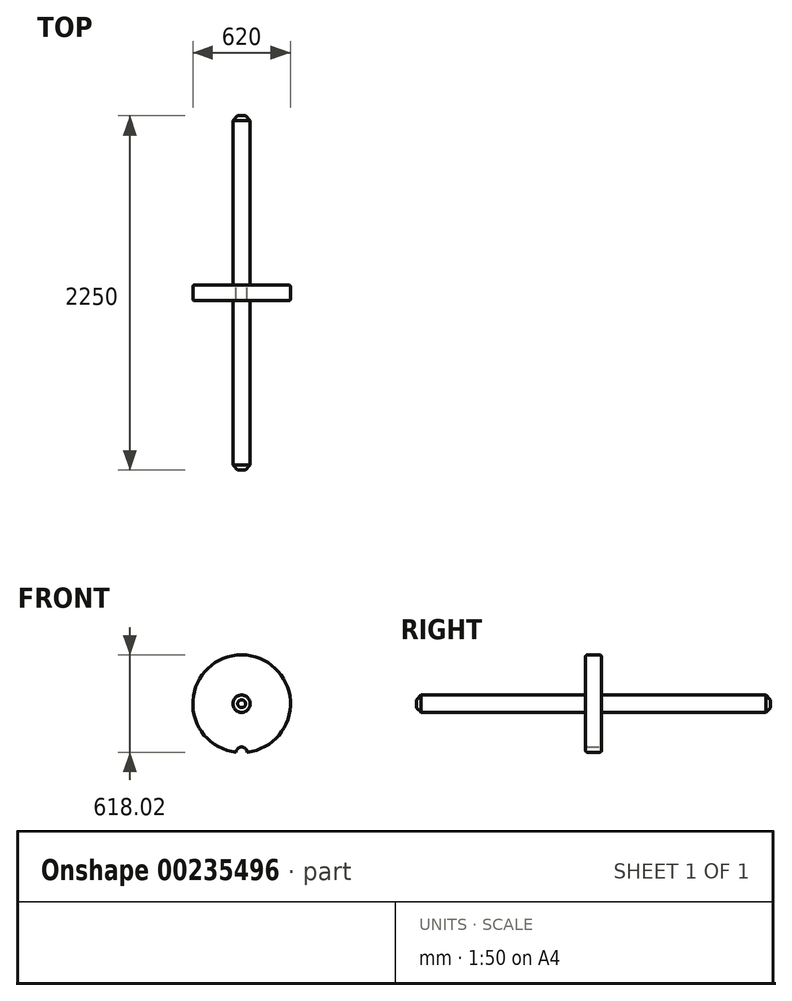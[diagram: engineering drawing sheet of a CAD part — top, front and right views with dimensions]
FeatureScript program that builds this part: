
annotation { "Feature Type Name" : "Feature", "Feature Type Description" : "" }
export const myFeature = defineFeature(function(context is Context, id is Id, definition is map)
    precondition{}
    {
        {
            var Q0;
            Q0=qCreatedBy(makeId("Front.planeOp"),FACE);
            var sketch = newSketch(context, id + "F0", { "sketchPlane" : qUnion([Q0])});
            skCircle(sketch, "E0", {"center": v(0, 0) * mm, "radius": 310 * mm});
            skCircle(sketch, "E1", {"center": v(0, 0) * mm, "radius": 55 * mm});
            skCircle(sketch, "E2", {"center": v(0, 0) * mm, "radius": 275 * mm, "construction": true});
            skSolve(sketch);
        }
        {
            var Q0;
            Q0=makeQuery(id+"F0.imprint","IMPRINT",FACE,{"disambiguationData":[TD([[makeQuery(id+"F0.imprint","IMPRINT",EDGE,{"derivedFrom":sQuery(id+"F0.wireOp",EDGE,"E0")}),1.0]])]});
            extrude(context, id + "F1", {"entities" : qUnion([Q0]), "endBound" : BoundingType.SYMMETRIC, "depth" : 100 * mm});
        }
        {
            var Q0;
            Q0=makeQuery(id+"F0.imprint","IMPRINT",FACE,{"disambiguationData":[TD([[makeQuery(id+"F0.imprint","IMPRINT",EDGE,{"derivedFrom":sQuery(id+"F0.wireOp",EDGE,"E1")}),1.0]])]});
            extrude(context, id + "F2", {"entities" : qUnion([Q0]), "operationType" : NewBodyOperationType.ADD, "endBound" : BoundingType.SYMMETRIC, "depth" : 2250 * mm});
        }
        {
            var Q0;
            Q0=makeQuery(id+"F2.opExtrude","CAP_EDGE",EDGE,{"disambiguationData":[OSD([sQuery(id+"F0.wireOp",EDGE,"E1")])],"isStart":false});
            var Q1;
            Q1=makeQuery(id+"F2.opExtrude","CAP_EDGE",EDGE,{"disambiguationData":[OSD([sQuery(id+"F0.wireOp",EDGE,"E1")])],"isStart":true});
            chamfer(context, id + "F3", {"entities" : qUnion([Q0, Q1]), "width" : 30 * mm, "tangentPropagation" : true});
        }
        {
            var Q0;
            Q0=makeQuery(id+"F1.opExtrude","CAP_FACE",FACE,{"disambiguationData":[OSD([sQuery(id+"F0.wireOp",EDGE,"E0"),sQuery(id+"F0.wireOp",EDGE,"E1")])],"isStart":true});
            var sketch = newSketch(context, id + "F4", { "sketchPlane" : qUnion([Q0])});
            skCircle(sketch, "E3", {"center": v(0, 0) * mm, "radius": 275 * mm});
            skCircle(sketch, "E4", {"center": v(0, -310) * mm, "radius": 35 * mm});
            skSolve(sketch);
        }
        {
            var Q0;
            {var subQ0=sQuery(id+"F4.wireOp",EDGE,"E4");var subQ1=makeQuery(id+"F4.imprint","INTERSECT",VERTEX,{"derivedFrom":[sQuery(id+"F4.wireOp",EDGE,"E3"),subQ0]});Q0=makeQuery(id+"F4.imprint","IMPRINT",FACE,{"disambiguationData":[TD([[makeQuery(id+"F4.imprint","IMPRINT",EDGE,{"disambiguationData":[TD([[subQ1,1.0]])],"derivedFrom":subQ0}),1.0]])]});}
            extrude(context, id + "F5", {"entities" : qUnion([Q0]), "operationType" : NewBodyOperationType.REMOVE, "oppositeDirection" : true, "depth" : 100 * mm});
        }
        {
            var Q0;
            Q0=makeQuery(id+"F1.opExtrude","CAP_FACE",FACE,{"disambiguationData":[OSD([sQuery(id+"F0.wireOp",EDGE,"E0"),sQuery(id+"F0.wireOp",EDGE,"E1")])],"isStart":true});
            fillet(context, id + "F6", {"entities" : qUnion([Q0]), "radius" : 10 * mm, "tangentPropagation" : true, "allowEdgeOverflow" : false});
        }
        {
            var Q0;
            Q0=makeQuery(id+"F1.opExtrude","CAP_FACE",FACE,{"disambiguationData":[OSD([sQuery(id+"F0.wireOp",EDGE,"E0"),sQuery(id+"F0.wireOp",EDGE,"E1")])],"isStart":false});
            fillet(context, id + "F7", {"entities" : qUnion([Q0]), "radius" : 10 * mm, "tangentPropagation" : true, "allowEdgeOverflow" : false});
        }
    });
